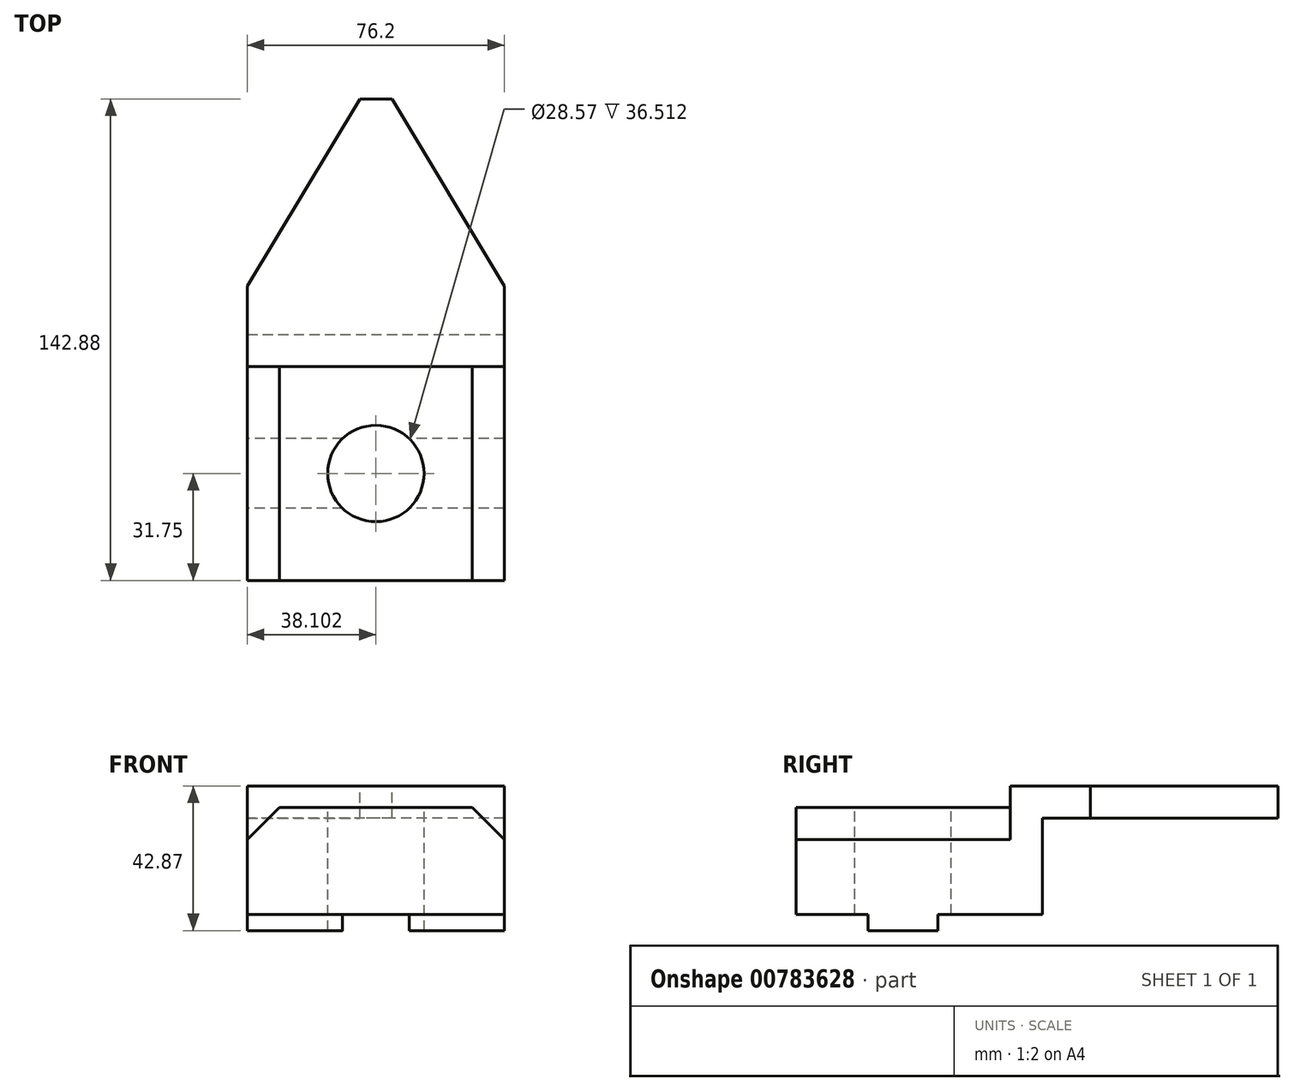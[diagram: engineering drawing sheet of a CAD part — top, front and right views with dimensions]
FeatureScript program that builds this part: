
annotation { "Feature Type Name" : "Feature", "Feature Type Description" : "" }
export const myFeature = defineFeature(function(context is Context, id is Id, definition is map)
    precondition{}
    {
        {
            var Q0;
            Q0=qCreatedBy(makeId("Front.planeOp"),FACE);
            var sketch = newSketch(context, id + "F0", { "sketchPlane" : qUnion([Q0])});
            skLineSegment(sketch, "E0", {"start": v(-48.82, -45.3) * mm, "end": v(27.38, -45.3) * mm});
            skLineSegment(sketch, "E1", {"start": v(27.38, -45.3) * mm, "end": v(27.38, -18.32) * mm});
            skLineSegment(sketch, "E2", {"start": v(-48.82, -45.3) * mm, "end": v(-48.82, -18.32) * mm});
            skLineSegment(sketch, "E3", {"start": v(-39.3, -8.8) * mm, "end": v(17.86, -8.8) * mm});
            skLineSegment(sketch, "E4", {"start": v(17.86, -8.8) * mm, "end": v(27.38, -18.32) * mm});
            skLineSegment(sketch, "E5", {"start": v(-39.3, -8.8) * mm, "end": v(-48.82, -18.32) * mm});
            skPoint(sketch, "E6.end.orphan", {"position": v(-39.3, -18.32) * mm});
            skPoint(sketch, "E7.orphan", {"position": v(-48.82, -8.8) * mm});
            skPoint(sketch, "E8.orphan", {"position": v(27.38, -8.8) * mm});
            skSolve(sketch);
        }
        {
            var Q0;
            Q0 = qSketchRegion(id + "F0", true);
            extrude(context, id + "F1", {"entities" : qUnion([Q0]), "depth" : 63.5 * mm, "offsetDistance" : 25.4 * mm});
        }
        {
            var Q0;
            Q0=makeQuery(id+"F1.opExtrude","CAP_FACE",FACE,{"disambiguationData":[OSD([sQuery(id+"F0.wireOp",EDGE,"E0"),sQuery(id+"F0.wireOp",EDGE,"E1"),sQuery(id+"F0.wireOp",EDGE,"E2"),sQuery(id+"F0.wireOp",EDGE,"E3"),sQuery(id+"F0.wireOp",EDGE,"E4"),sQuery(id+"F0.wireOp",EDGE,"E5")])],"isStart":false});
            var sketch = newSketch(context, id + "F2", { "sketchPlane" : qUnion([Q0])});
            skLineSegment(sketch, "E9", {"start": v(-48.82, -45.3) * mm, "end": v(-48.82, -40.54) * mm});
            skLineSegment(sketch, "E10", {"start": v(-48.82, -40.54) * mm, "end": v(27.38, -40.54) * mm});
            skSolve(sketch);
        }
        {
            var Q0;
            Q0 = qSketchRegion(id + "F2", true);
            var Q1;
            Q1=makeQuery(id+"F2.imprint","IMPRINT",FACE,{"disambiguationData":[TD([[makeQuery(id+"F2.imprint","IMPRINT",EDGE,{"derivedFrom":sQuery(id+"F2.wireOp",EDGE,"E9")}),-1.0]])]});
            extrude(context, id + "F3", {"entities" : qUnion([Q0, Q1]), "operationType" : NewBodyOperationType.REMOVE, "oppositeDirection" : true, "depth" : 103.38 * mm, "offsetDistance" : 25.4 * mm});
        }
        {
            var Q0;
            Q0=makeQuery(id+"F1.opExtrude","CAP_FACE",FACE,{"disambiguationData":[OSD([sQuery(id+"F0.wireOp",EDGE,"E0"),sQuery(id+"F0.wireOp",EDGE,"E1"),sQuery(id+"F0.wireOp",EDGE,"E2"),sQuery(id+"F0.wireOp",EDGE,"E3"),sQuery(id+"F0.wireOp",EDGE,"E4"),sQuery(id+"F0.wireOp",EDGE,"E5")])],"isStart":true});
            var sketch = newSketch(context, id + "F4", { "sketchPlane" : qUnion([Q0])});
            skSolve(sketch);
        }
        {
            var Q0;
            {var subQ2=sQuery(id+"F0.wireOp",EDGE,"E3");Q0=makeQuery(id+"F4.imprint","IMPRINT",FACE,{"disambiguationData":[TD([[makeQuery(id+"F4.imprint","IMPRINT",EDGE,{"derivedFrom":makeQuery(id+"F1.opExtrude","CAP_EDGE",EDGE,{"disambiguationData":[OSD([subQ2])],"isStart":true})}),1.0]])]});}
            extrude(context, id + "F5", {"entities" : qUnion([Q0]), "operationType" : NewBodyOperationType.ADD, "depth" : 9.52 * mm, "offsetDistance" : 25.4 * mm});
        }
        {
            var Q0;
            {var subQ0=sQuery(id+"F0.wireOp",EDGE,"E3");Q0=makeQuery(id+"F5.boolean.opBoolean","MERGE",FACE,{"derivedFrom":[makeQuery(id+"F1.opExtrude","SWEPT_FACE",FACE,{"disambiguationData":[OSD([subQ0])]}),makeQuery(id+"F5.opExtrude","SWEPT_FACE",FACE,{"disambiguationData":[OSD([subQ0])]})]});}
            var sketch = newSketch(context, id + "F6", { "sketchPlane" : qUnion([Q0])});
            skLineSegment(sketch, "E11", {"start": v(17.86, 9.53) * mm, "end": v(17.86, 0) * mm});
            skLineSegment(sketch, "E12", {"start": v(17.86, 0) * mm, "end": v(-39.3, 0) * mm});
            skSolve(sketch);
        }
        {
            var Q0;
            Q0 = qSketchRegion(id + "F6", true);
            var Q1;
            Q1=makeQuery(id+"F6.imprint","IMPRINT",FACE,{"disambiguationData":[TD([[makeQuery(id+"F6.imprint","IMPRINT",EDGE,{"derivedFrom":sQuery(id+"F6.wireOp",EDGE,"E11")}),1.0]])]});
            extrude(context, id + "F7", {"entities" : qUnion([Q0, Q1]), "operationType" : NewBodyOperationType.ADD, "depth" : 6.35 * mm, "offsetDistance" : 25.4 * mm});
        }
        {
            var Q0;
            {var subQ0=sQuery(id+"F0.wireOp",EDGE,"E3");Q0=makeQuery(id+"F7.boolean.opBoolean","MERGE",FACE,{"derivedFrom":[makeQuery(id+"F5.opExtrude","CAP_FACE",FACE,{"disambiguationData":[OSD([sQuery(id+"F0.wireOp",EDGE,"E0"),sQuery(id+"F0.wireOp",EDGE,"E1"),sQuery(id+"F0.wireOp",EDGE,"E2"),subQ0,sQuery(id+"F0.wireOp",EDGE,"E4"),sQuery(id+"F0.wireOp",EDGE,"E5"),sQuery(id+"F2.wireOp",EDGE,"E10")])],"isStart":false}),makeQuery(id+"F7.opExtrude","SWEPT_FACE",FACE,{"disambiguationData":[OSD([subQ0])]})]});}
            var sketch = newSketch(context, id + "F8", { "sketchPlane" : qUnion([Q0])});
            skLineSegment(sketch, "E13", {"start": v(-17.86, -2.44) * mm, "end": v(-17.86, -11.97) * mm});
            skPoint(sketch, "E13.endSnap0", {"position": v(-17.86, -5.62) * mm});
            skLineSegment(sketch, "E14", {"start": v(-17.86, -2.44) * mm, "end": v(-27.38, -2.44) * mm});
            skLineSegment(sketch, "E15", {"start": v(-27.38, -2.44) * mm, "end": v(-27.38, -18.32) * mm});
            skLineSegment(sketch, "E16", {"start": v(48.82, -18.32) * mm, "end": v(48.82, -2.44) * mm});
            skLineSegment(sketch, "E17", {"start": v(48.82, -2.44) * mm, "end": v(39.3, -2.44) * mm});
            skSolve(sketch);
        }
        {
            var Q0;
            Q0 = qSketchRegion(id + "F8", true);
            var Q1;
            {var subQ0=sQuery(id+"F8.wireOp",EDGE,"E14");Q1=makeQuery(id+"F8.imprint","IMPRINT",FACE,{"disambiguationData":[TD([[makeQuery(id+"F8.imprint","IMPRINT",EDGE,{"derivedFrom":subQ0}),1.0]])]});}
            var Q2;
            Q2=makeQuery(id+"F8.imprint","IMPRINT",FACE,{"disambiguationData":[TD([[makeQuery(id+"F8.imprint","IMPRINT",EDGE,{"derivedFrom":sQuery(id+"F8.wireOp",EDGE,"E16")}),1.0]])]});
            extrude(context, id + "F9", {"entities" : qUnion([Q0, Q1, Q2]), "operationType" : NewBodyOperationType.ADD, "oppositeDirection" : true, "depth" : 9.52 * mm, "offsetDistance" : 25.4 * mm});
        }
        {
            var Q0;
            {var subQ0=sQuery(id+"F0.wireOp",EDGE,"E5");var subQ1=sQuery(id+"F0.wireOp",EDGE,"E3");var subQ2=sQuery(id+"F0.wireOp",EDGE,"E4");Q0=makeQuery(id+"F9.boolean.opBoolean","MERGE",FACE,{"derivedFrom":[makeQuery(id+"F7.boolean.opBoolean","MERGE",FACE,{"derivedFrom":[makeQuery(id+"F5.opExtrude","CAP_FACE",FACE,{"disambiguationData":[OSD([sQuery(id+"F0.wireOp",EDGE,"E0"),sQuery(id+"F0.wireOp",EDGE,"E1"),sQuery(id+"F0.wireOp",EDGE,"E2"),subQ1,subQ2,subQ0,sQuery(id+"F2.wireOp",EDGE,"E10")])],"isStart":false}),makeQuery(id+"F7.opExtrude","SWEPT_FACE",FACE,{"disambiguationData":[OSD([subQ1])]})]}),makeQuery(id+"F9.opExtrude","CAP_FACE",FACE,{"disambiguationData":[OSD([subQ2,sQuery(id+"F8.wireOp",EDGE,"E13"),sQuery(id+"F8.wireOp",EDGE,"E14"),sQuery(id+"F8.wireOp",EDGE,"E15")])],"isStart":true}),makeQuery(id+"F9.opExtrude","CAP_FACE",FACE,{"disambiguationData":[OSD([subQ1,subQ0,sQuery(id+"F8.wireOp",EDGE,"E16"),sQuery(id+"F8.wireOp",EDGE,"E17")])],"isStart":true})]});}
            var sketch = newSketch(context, id + "F10", { "sketchPlane" : qUnion([Q0])});
            skLineSegment(sketch, "E18", {"start": v(-27.38, -2.44) * mm, "end": v(-27.38, -11.97) * mm});
            skLineSegment(sketch, "E19", {"start": v(-27.38, -11.97) * mm, "end": v(48.82, -11.97) * mm});
            skSolve(sketch);
        }
        {
            var Q0;
            Q0 = qSketchRegion(id + "F10", true);
            var Q1;
            Q1=makeQuery(id+"F10.imprint","IMPRINT",FACE,{"disambiguationData":[TD([[makeQuery(id+"F10.imprint","IMPRINT",EDGE,{"derivedFrom":sQuery(id+"F10.wireOp",EDGE,"E18")}),-1.0]])]});
            extrude(context, id + "F11", {"entities" : qUnion([Q0, Q1]), "operationType" : NewBodyOperationType.ADD, "depth" : 23.8 * mm, "offsetDistance" : 25.4 * mm});
        }
        {
            var Q0;
            Q0=makeQuery(id+"F11.opExtrude","CAP_FACE",FACE,{"disambiguationData":[OSD([sQuery(id+"F0.wireOp",EDGE,"E2"),sQuery(id+"F0.wireOp",EDGE,"E3"),sQuery(id+"F8.wireOp",EDGE,"E14"),sQuery(id+"F8.wireOp",EDGE,"E16"),sQuery(id+"F8.wireOp",EDGE,"E17"),sQuery(id+"F10.wireOp",EDGE,"E18"),sQuery(id+"F10.wireOp",EDGE,"E19")])],"isStart":false});
            var sketch = newSketch(context, id + "F12", { "sketchPlane" : qUnion([Q0])});
            skSolve(sketch);
        }
        {
            var Q0;
            Q0 = qSketchRegion(id + "F12", true);
            var Q1;
            Q1=makeQuery(id+"F12.imprint","IMPRINT",FACE,{"disambiguationData":[TD([[makeQuery(id+"F12.imprint","IMPRINT",EDGE,{"derivedFrom":makeQuery(id+"F11.opExtrude","CAP_EDGE",EDGE,{"disambiguationData":[OSD([sQuery(id+"F10.wireOp",EDGE,"E18")])],"isStart":false})}),-1.0]])]});
            extrude(context, id + "F13", {"entities" : qUnion([Q0, Q1]), "operationType" : NewBodyOperationType.ADD, "depth" : 46.04 * mm, "offsetDistance" : 25.4 * mm});
        }
        {
            var Q0;
            {var subQ0=sQuery(id+"F8.wireOp",EDGE,"E17");var subQ1=sQuery(id+"F8.wireOp",EDGE,"E14");var subQ2=sQuery(id+"F0.wireOp",EDGE,"E3");Q0=makeQuery(id+"F13.boolean.opBoolean","MERGE",FACE,{"derivedFrom":[makeQuery(id+"F11.boolean.opBoolean","MERGE",FACE,{"derivedFrom":[makeQuery(id+"F9.boolean.opBoolean","MERGE",FACE,{"derivedFrom":[makeQuery(id+"F7.opExtrude","CAP_FACE",FACE,{"disambiguationData":[OSD([subQ2,sQuery(id+"F0.wireOp",EDGE,"E5"),sQuery(id+"F6.wireOp",EDGE,"E11"),sQuery(id+"F6.wireOp",EDGE,"E12")])],"isStart":false}),makeQuery(id+"F9.opExtrude","SWEPT_FACE",FACE,{"disambiguationData":[OSD([subQ1])]}),makeQuery(id+"F9.opExtrude","SWEPT_FACE",FACE,{"disambiguationData":[OSD([subQ0])]})]}),makeQuery(id+"F11.opExtrude","SWEPT_FACE",FACE,{"disambiguationData":[OSD([subQ2,subQ1,subQ0])]})]}),makeQuery(id+"F13.opExtrude","SWEPT_FACE",FACE,{"disambiguationData":[OSD([subQ2,subQ1,subQ0])]})]});}
            var sketch = newSketch(context, id + "F14", { "sketchPlane" : qUnion([Q0])});
            skLineSegment(sketch, "E20", {"start": v(-10.72, 79.38) * mm, "end": v(-5.96, 79.38) * mm});
            skLineSegment(sketch, "E21", {"start": v(-10.72, 79.38) * mm, "end": v(-15.48, 79.38) * mm});
            skLineSegment(sketch, "E22", {"start": v(-48.82, 0) * mm, "end": v(-48.82, 23.81) * mm});
            skLineSegment(sketch, "E23", {"start": v(-48.82, 23.81) * mm, "end": v(27.38, 23.81) * mm});
            skLineSegment(sketch, "E24", {"start": v(-48.82, 23.81) * mm, "end": v(-15.48, 79.38) * mm});
            skLineSegment(sketch, "E25", {"start": v(27.38, 23.81) * mm, "end": v(-5.96, 79.38) * mm});
            skSolve(sketch);
        }
        {
            var Q0;
            {var subQ0=sQuery(id+"F14.wireOp",EDGE,"E24");Q0=makeQuery(id+"F14.imprint","IMPRINT",FACE,{"disambiguationData":[TD([[makeQuery(id+"F14.imprint","IMPRINT",EDGE,{"derivedFrom":subQ0}),1.0]])]});}
            var Q1;
            {var subQ0=sQuery(id+"F14.wireOp",EDGE,"E25");Q1=makeQuery(id+"F14.imprint","IMPRINT",FACE,{"disambiguationData":[TD([[makeQuery(id+"F14.imprint","IMPRINT",EDGE,{"derivedFrom":subQ0}),-1.0]])]});}
            extrude(context, id + "F15", {"entities" : qUnion([Q0, Q1]), "operationType" : NewBodyOperationType.REMOVE, "oppositeDirection" : true, "depth" : 25.4 * mm, "offsetDistance" : 25.4 * mm});
        }
        {
            var Q0;
            {var subQ0=sQuery(id+"F2.wireOp",EDGE,"E10");Q0=makeQuery(id+"F5.boolean.opBoolean","MERGE",FACE,{"derivedFrom":[makeQuery(id+"F3.boolean.opBoolean","COPY",FACE,{"derivedFrom":makeQuery(id+"F3.opExtrude","SWEPT_FACE",FACE,{"disambiguationData":[OSD([subQ0])]})}),makeQuery(id+"F5.opExtrude","SWEPT_FACE",FACE,{"disambiguationData":[OSD([sQuery(id+"F0.wireOp",EDGE,"E0"),sQuery(id+"F0.wireOp",EDGE,"E1"),sQuery(id+"F0.wireOp",EDGE,"E2"),sQuery(id+"F0.wireOp",EDGE,"E3"),sQuery(id+"F0.wireOp",EDGE,"E4"),sQuery(id+"F0.wireOp",EDGE,"E5"),subQ0])]})]});}
            var sketch = newSketch(context, id + "F16", { "sketchPlane" : qUnion([Q0])});
            skLineSegment(sketch, "E26", {"start": v(27.38, 63.5) * mm, "end": v(27.38, 31.75) * mm});
            skLineSegment(sketch, "E27", {"start": v(27.38, 31.75) * mm, "end": v(27.38, 21.43) * mm});
            skLineSegment(sketch, "E28", {"start": v(27.38, 31.75) * mm, "end": v(27.38, 42.06) * mm});
            skLineSegment(sketch, "E29", {"start": v(27.38, 42.06) * mm, "end": v(-48.82, 42.06) * mm});
            skLineSegment(sketch, "E30", {"start": v(27.38, 21.43) * mm, "end": v(-48.82, 21.43) * mm});
            skSolve(sketch);
        }
        {
            var Q0;
            Q0 = qSketchRegion(id + "F16", true);
            var Q1;
            Q1=makeQuery(id+"F16.imprint","IMPRINT",FACE,{"disambiguationData":[TD([[makeQuery(id+"F16.imprint","IMPRINT",EDGE,{"derivedFrom":sQuery(id+"F16.wireOp",EDGE,"E27")}),1.0]])]});
            extrude(context, id + "F17", {"entities" : qUnion([Q0, Q1]), "operationType" : NewBodyOperationType.ADD, "depth" : 4.76 * mm, "offsetDistance" : 25.4 * mm});
        }
        {
            var Q0;
            {var subQ0=sQuery(id+"F0.wireOp",EDGE,"E3");Q0=makeQuery(id+"F5.boolean.opBoolean","MERGE",FACE,{"derivedFrom":[makeQuery(id+"F1.opExtrude","SWEPT_FACE",FACE,{"disambiguationData":[OSD([subQ0])]}),makeQuery(id+"F5.opExtrude","SWEPT_FACE",FACE,{"disambiguationData":[OSD([subQ0])]})]});}
            var sketch = newSketch(context, id + "F18", { "sketchPlane" : qUnion([Q0])});
            skLineSegment(sketch, "E31", {"start": v(-10.72, -63.5) * mm, "end": v(-10.72, -31.75) * mm});
            skCircle(sketch, "E32", {"center": v(-10.72, -31.75) * mm, "radius": 14.29 * mm});
            skSolve(sketch);
        }
        {
            var Q0;
            Q0 = qSketchRegion(id + "F18", true);
            extrude(context, id + "F19", {"entities" : qUnion([Q0]), "operationType" : NewBodyOperationType.REMOVE, "oppositeDirection" : true, "depth" : 54.36 * mm, "offsetDistance" : 25.4 * mm});
        }
    });
